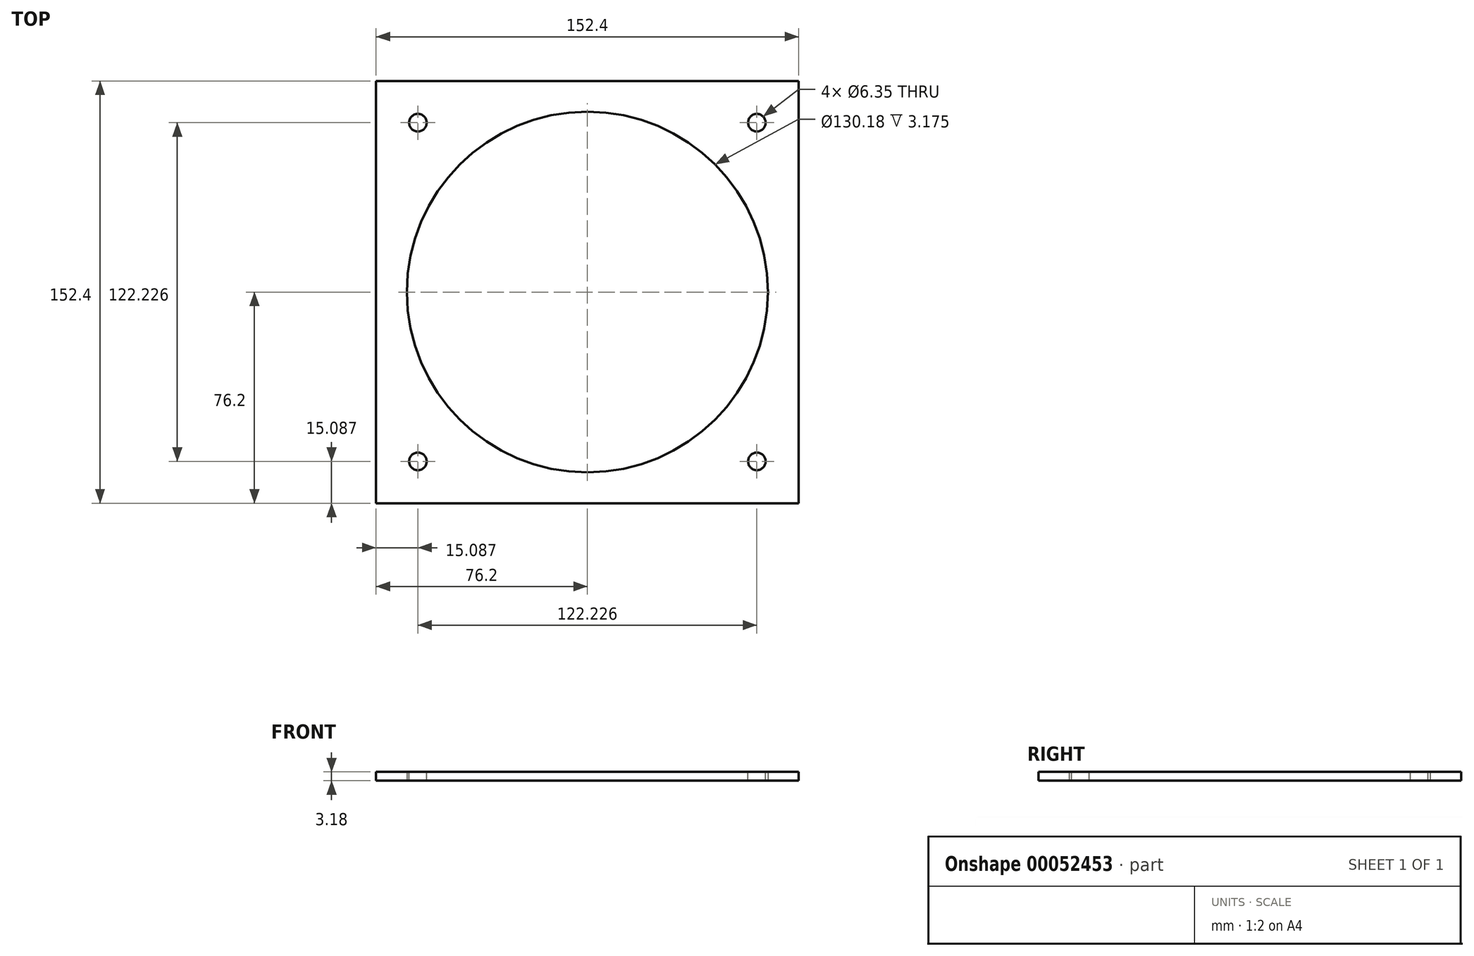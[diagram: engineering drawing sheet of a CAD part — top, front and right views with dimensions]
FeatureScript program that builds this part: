
annotation { "Feature Type Name" : "Feature", "Feature Type Description" : "" }
export const myFeature = defineFeature(function(context is Context, id is Id, definition is map)
    precondition{}
    {
        {
            var Q0;
            Q0=qCreatedBy(makeId("Top.planeOp"),FACE);
            var sketch = newSketch(context, id + "F0", { "sketchPlane" : qUnion([Q0])});
            skCircle(sketch, "E0", {"center": v(0, 0) * mm, "radius": 65.09 * mm});
            skLineSegment(sketch, "E1.rect.bottom", {"start": v(76.2, -76.2) * mm, "end": v(-76.2, -76.2) * mm});
            skLineSegment(sketch, "E1.rect.top", {"start": v(76.2, 76.2) * mm, "end": v(-76.2, 76.2) * mm});
            skLineSegment(sketch, "E1.rect.left", {"start": v(76.2, -76.2) * mm, "end": v(76.2, 76.2) * mm});
            skLineSegment(sketch, "E1.rect.right", {"start": v(-76.2, -76.2) * mm, "end": v(-76.2, 76.2) * mm});
            skSolve(sketch);
        }
        {
            var Q0;
            Q0 = qSketchRegion(id + "F0", true);
            var Q1;
            Q1=makeQuery(id+"F0.imprint","IMPRINT",FACE,{"disambiguationData":[TD([[makeQuery(id+"F0.imprint","IMPRINT",EDGE,{"derivedFrom":sQuery(id+"F0.wireOp",EDGE,"E0")}),-1.0]])]});
            extrude(context, id + "F1", {"entities" : qUnion([Q0, Q1]), "depth" : 3.17 * mm});
        }
        {
            var Q0;
            Q0=makeQuery(id+"F1.opExtrude","CAP_FACE",FACE,{"disambiguationData":[OSD([sQuery(id+"F0.wireOp",EDGE,"E0"),sQuery(id+"F0.wireOp",EDGE,"E1.rect.bottom"),sQuery(id+"F0.wireOp",EDGE,"E1.rect.top"),sQuery(id+"F0.wireOp",EDGE,"E1.rect.left"),sQuery(id+"F0.wireOp",EDGE,"E1.rect.right")])],"isStart":false});
            var sketch = newSketch(context, id + "F2", { "sketchPlane" : qUnion([Q0])});
            skCircle(sketch, "E2", {"center": v(-61.11, 61.11) * mm, "radius": 3.18 * mm});
            skCircle(sketch, "E3", {"center": v(61.11, 61.11) * mm, "radius": 3.18 * mm});
            skCircle(sketch, "E4", {"center": v(61.11, -61.11) * mm, "radius": 3.18 * mm});
            skCircle(sketch, "E5", {"center": v(-61.11, -61.11) * mm, "radius": 3.18 * mm});
            skSolve(sketch);
        }
        {
            var Q0;
            Q0=sQuery(id+"F2.wireOp",VERTEX,"E5.center");
            var Q1;
            Q1=sQuery(id+"F2.wireOp",VERTEX,"E4.center");
            var Q2;
            Q2=sQuery(id+"F2.wireOp",VERTEX,"E3.center");
            var Q3;
            Q3=sQuery(id+"F2.wireOp",VERTEX,"E2.center");
            var Q4;
            Q4=makeQuery(id+"F1.opExtrude","SWEPT_BODY",BODY,{"disambiguationData":[OSD([sQuery(id+"F0.wireOp",EDGE,"E0"),sQuery(id+"F0.wireOp",EDGE,"E1.rect.bottom"),sQuery(id+"F0.wireOp",EDGE,"E1.rect.top"),sQuery(id+"F0.wireOp",EDGE,"E1.rect.left"),sQuery(id+"F0.wireOp",EDGE,"E1.rect.right")])]});
            hole(context, id + "F3", {"style" : HoleStyle.SIMPLE, "holeDiameter" : 6.35 * mm, "endStyle" : HoleEndStyle.THROUGH, "locations" : qUnion([Q0, Q1, Q2, Q3]), "scope" : qUnion([Q4])});
        }
    });
